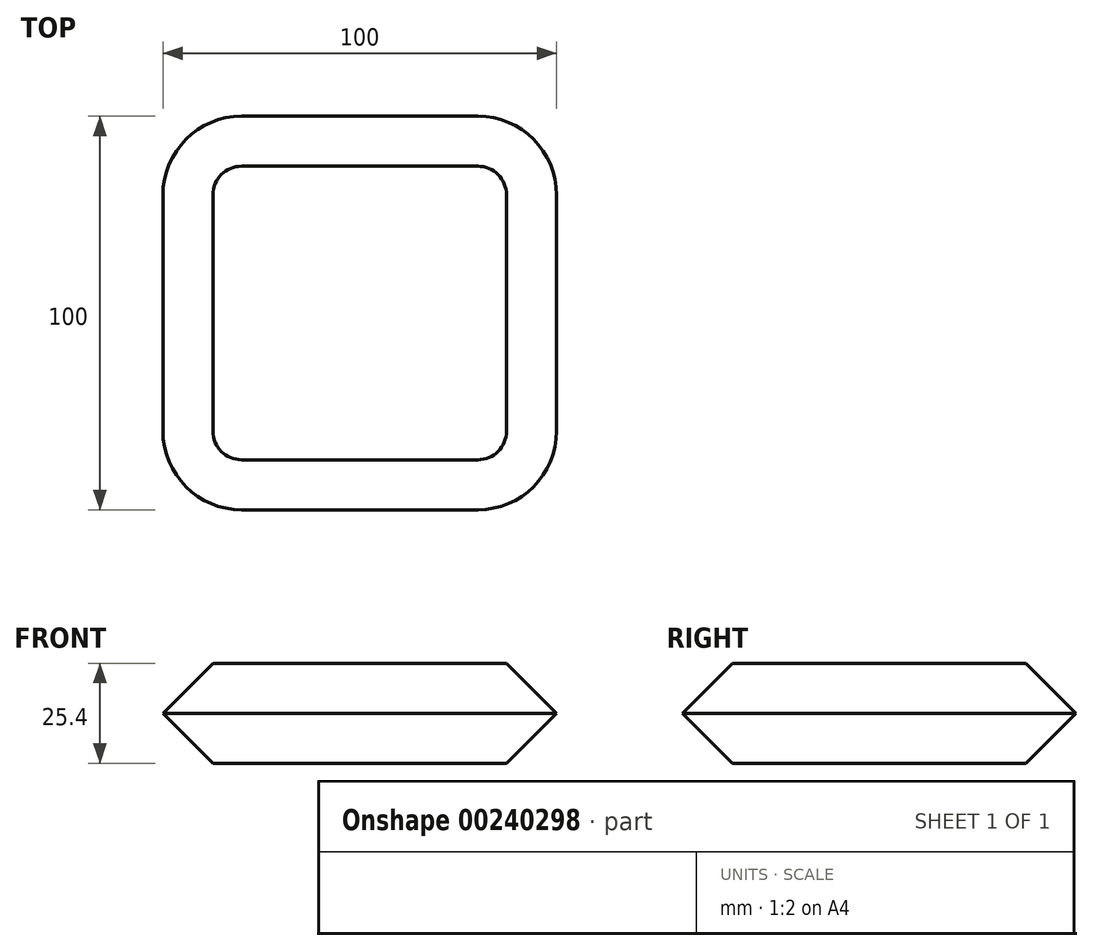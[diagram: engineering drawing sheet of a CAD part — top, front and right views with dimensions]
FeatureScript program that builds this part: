
annotation { "Feature Type Name" : "Feature", "Feature Type Description" : "" }
export const myFeature = defineFeature(function(context is Context, id is Id, definition is map)
    precondition{}
    {
        {
            var Q0;
            Q0=qCreatedBy(makeId("Top.planeOp"),FACE);
            var sketch = newSketch(context, id + "F0", { "sketchPlane" : qUnion([Q0])});
            skLineSegment(sketch, "E0.bottom", {"start": v(30, -50) * mm, "end": v(-30, -50) * mm});
            skLineSegment(sketch, "E0.top", {"start": v(30, 50) * mm, "end": v(-30, 50) * mm});
            skLineSegment(sketch, "E0.left", {"start": v(50, -30) * mm, "end": v(50, 30) * mm});
            skLineSegment(sketch, "E0.right", {"start": v(-50, -30) * mm, "end": v(-50, 30) * mm});
            skPoint(sketch, "E0.middle", {"position": v(0, 0) * mm});
            skPoint(sketch, "E1.visualSharp", {"position": v(-50, 50) * mm});
            skArc(sketch, "E1.filletArc", {"start": v(-30, 50) * mm, "mid": v(-44.14, 44.14) * mm, "end": v(-50, 30) * mm});
            skPoint(sketch, "E2.visualSharp", {"position": v(50, 50) * mm});
            skArc(sketch, "E2.filletArc", {"start": v(50, 30) * mm, "mid": v(44.14, 44.14) * mm, "end": v(30, 50) * mm});
            skPoint(sketch, "E3.visualSharp", {"position": v(50, -50) * mm});
            skArc(sketch, "E3.filletArc", {"start": v(30, -50) * mm, "mid": v(44.14, -44.14) * mm, "end": v(50, -30) * mm});
            skPoint(sketch, "E4.visualSharp", {"position": v(-50, -50) * mm});
            skArc(sketch, "E4.filletArc", {"start": v(-50, -30) * mm, "mid": v(-44.14, -44.14) * mm, "end": v(-30, -50) * mm});
            skSolve(sketch);
        }
        {
            var Q0;
            Q0 = qSketchRegion(id + "FWTJm7pjlG4kkUz_0", true);
            var Q1;
            Q1=makeQuery(id+"F0.imprint","IMPRINT",FACE,{"disambiguationData":[TD([[makeQuery(id+"F0.imprint","IMPRINT",EDGE,{"derivedFrom":sQuery(id+"F0.wireOp",EDGE,"E0.bottom")}),-1.0]])]});
            extrude(context, id + "F1", {"entities" : qUnion([Q0, Q1]), "depth" : 25.4 * mm});
        }
        {
            var Q0;
            Q0=makeQuery(id+"F1.opExtrude","CAP_FACE",FACE,{"disambiguationData":[OSD([sQuery(id+"F0.wireOp",EDGE,"E0.bottom"),sQuery(id+"F0.wireOp",EDGE,"E0.top"),sQuery(id+"F0.wireOp",EDGE,"E0.left"),sQuery(id+"F0.wireOp",EDGE,"E0.right"),sQuery(id+"F0.wireOp",EDGE,"E1.filletArc"),sQuery(id+"F0.wireOp",EDGE,"E2.filletArc"),sQuery(id+"F0.wireOp",EDGE,"E3.filletArc"),sQuery(id+"F0.wireOp",EDGE,"E4.filletArc")])],"isStart":true});
            var Q1;
            Q1=makeQuery(id+"F1.opExtrude","CAP_FACE",FACE,{"disambiguationData":[OSD([sQuery(id+"F0.wireOp",EDGE,"E0.bottom"),sQuery(id+"F0.wireOp",EDGE,"E0.top"),sQuery(id+"F0.wireOp",EDGE,"E0.left"),sQuery(id+"F0.wireOp",EDGE,"E0.right"),sQuery(id+"F0.wireOp",EDGE,"E1.filletArc"),sQuery(id+"F0.wireOp",EDGE,"E2.filletArc"),sQuery(id+"F0.wireOp",EDGE,"E3.filletArc"),sQuery(id+"F0.wireOp",EDGE,"E4.filletArc")])],"isStart":false});
            chamfer(context, id + "F2", {"entities" : qUnion([Q0, Q1]), "width" : 12.7 * mm, "tangentPropagation" : true});
        }
    });
